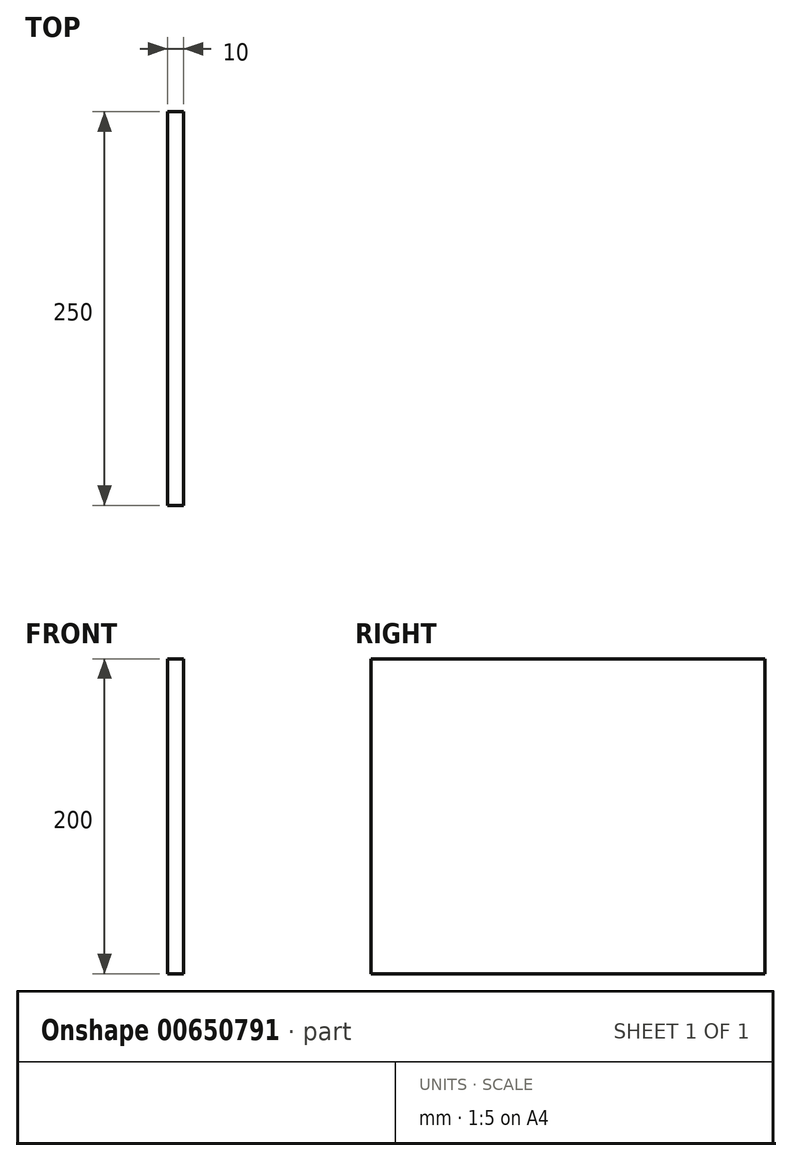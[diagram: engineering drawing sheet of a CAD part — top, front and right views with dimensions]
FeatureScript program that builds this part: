
annotation { "Feature Type Name" : "Feature", "Feature Type Description" : "" }
export const myFeature = defineFeature(function(context is Context, id is Id, definition is map)
    precondition{}
    {
        {
            var Q0;
            Q0=qCreatedBy(makeId("Right.planeOp"),FACE);
            var sketch = newSketch(context, id + "F0", { "sketchPlane" : qUnion([Q0])});
            skLineSegment(sketch, "E0.bottom", {"start": v(-92.1, 91.98) * mm, "end": v(157.9, 91.98) * mm});
            skLineSegment(sketch, "E0.top", {"start": v(-92.1, -108.02) * mm, "end": v(157.9, -108.02) * mm});
            skLineSegment(sketch, "E0.left", {"start": v(-92.1, 91.98) * mm, "end": v(-92.1, -108.02) * mm});
            skLineSegment(sketch, "E0.right", {"start": v(157.9, 91.98) * mm, "end": v(157.9, -108.02) * mm});
            skSolve(sketch);
        }
        {
            var Q0;
            Q0 = qSketchRegion(id + "F0", true);
            extrude(context, id + "F1", {"entities" : qUnion([Q0]), "depth" : 10 * mm, "offsetDistance" : 25 * mm});
        }
    });
